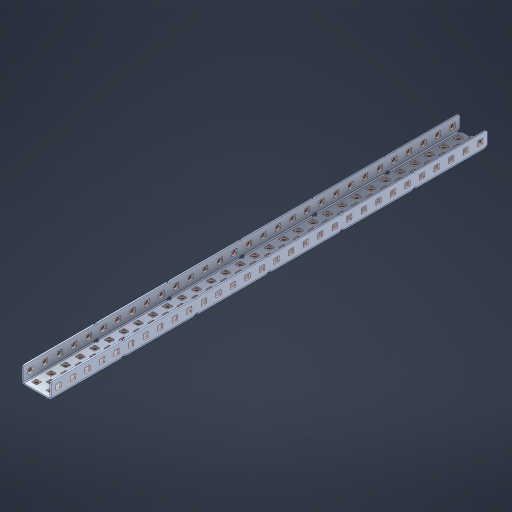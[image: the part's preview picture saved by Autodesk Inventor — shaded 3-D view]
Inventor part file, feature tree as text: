
AUTODESK INVENTOR PART (.ipt)
format: ipt  version: 2023 (Build 270158000, 158)  size: 1,864,704 bytes
history: native  units: in
note: dims shown in document units (in); Inventor stores cm internally (conversion verified against a paired STEP export)
features: other x157, extrude x148, sheet_metal_op x11, sketch x10, pattern_linear x2, mirror x1, chamfer x1
ambient origin geometry x8: Origin, YZ Plane, XZ Plane, XY Plane, X Axis, Y Axis, Z Axis, Center Point
bodies: Solid1 (feature_tree), Body (feature_tree)
feature tree (330):
  sheet_metal_op  "Flanges"
  other  "Flange Pattern Plane"
  other  "Flange Pattern Sketch"
  sheet_metal_op  "Flange Pattern"
  sheet_metal_op  "Body Pattern"
  pattern_linear  "Center Pattern"  Spacing1=0.0469in  [1 undecoded]
  other  "Arc Length"
  mirror  "Notch Mirror"
  pattern_linear  "Notch Pattern"  Spacing1=0.182in  [1 undecoded]
  chamfer  "End Chamfer"
  extrude  "Half Cut"  Depth=0.02in
  sketch  "Sketch1"  dims[d0=1.0in]
  other  "Plate1"
  sketch  "Sketch2"  dims[d1=15.0in]
  other  "Plate2"
  sheet_metal_op  "Bend1"
  sheet_metal_op  "Corner1"
  sketch  "Sketch3"  dims[d2=0.0469in]
  sketch  "Sketch7"  dims[d3=0.0469in]
  other  "Srf1"
  other  "Srf2"
  sketch  "Sketch8"  dims[d4=0.0234in]
  sketch  "Sketch9"  dims[d5=0.0938in]
  other  "Srf91"
  sheet_metal_op  "Body Pattern Sketch"
  other  "Srf92"
  sketch  "Sketch13"  dims[d6=0.0469in]
  sketch  "Sketch14"  dims[d7=0.5in d8=90.0deg d9=0.0312in]
  sketch  "Sketch15"  dims[d10=0.1875in]
  sketch  "Sketch16"  dims[d11=0.0469in d12=0.0469in d16=0.182in d17=0.02in d18=0.0469in d19=0.0in d20=0.25in d21=0.25in d38=11.811in d40=0.5in d41=0.7874in d43=1.0in d46=0.172in d47=1.0in d48=0.0in d49=0.182in d50=0.02in d51=0.25in d52=0.25in d53=0.0469in d54=0.0in d55=0.172in d56=1.0in d57=0.0in d58=0.25in d60=11.811in d62=0.5in d63=0.7874in d65=0.5in d85=0.1227in d86=0.1659in d88=0.04in d89=0.0469in d90=0.0in d91=0.04in d92=0.0491in d95=2.5in d96=0.04in d97=0.25in d98=45.0deg d99=0.25in d100=0.5in d101=0.0in d102=2.497in d106=0.182in d107=0.02in d108=0.5in d109=0.5in d110=0.0469in d111=0.0in d112=0.172in d113=0.5in d114=0.0in d117=0.5in d118=0.5in d119=0.5in]
  other  "Srf786"
  other  "Srf823"
  other  "Srf824"
  other  "Srf825"
  other  "Srf826"
  other  "Srf827"
  other  "Srf828"
  other  "Srf829"
  other  "Srf856"
  other  "Srf857"
  other  "Srf858"
  other  "Srf859"
  other  "Srf860"
  other  "Srf861"
  other  "Srf862"
  other  "Srf889"
  other  "Srf890"
  other  "Srf891"
  other  "Srf892"
  other  "Srf893"
  other  "Srf894"
  other  "Srf895"
  other  "Srf896"
  other  "Srf922"
  other  "Srf923"
  other  "Srf924"
  other  "Srf925"
  other  "Srf926"
  other  "Srf959"
  other  "Srf960"
  other  "Srf961"
  other  "Srf962"
  other  "Srf963"
  other  "Srf996"
  other  "Srf997"
  other  "Srf998"
  other  "Srf999"
  other  "Srf1000"
  other  "Srf1143"
  other  "Srf1144"
  other  "Srf1145"
  other  "Srf1146"
  other  "Srf1147"
  other  "Srf1148"
  other  "Srf1149"
  other  "Srf1150"
  other  "Srf1151"
  other  "Srf1152"
  other  "Srf1153"
  other  "Srf1154"
  other  "Srf1155"
  other  "Srf1156"
  other  "Srf1157"
  other  "Srf1158"
  other  "Srf1159"
  other  "Srf1160"
  other  "Srf1161"
  other  "Srf1162"
  other  "Srf1163"
  other  "Srf1164"
  other  "Srf1165"
  other  "Srf1166"
  other  "Srf1167"
  other  "Srf1168"
  other  "Srf1169"
  other  "Srf1170"
  other  "Srf1171"
  other  "Srf1172"
  other  "Srf1173"
  other  "Srf1174"
  other  "Srf1175"
  other  "Srf1176"
  other  "Srf1177"
  other  "Srf1178"
  other  "Srf1179"
  other  "Srf1180"
  other  "Srf1181"
  other  "Srf1182"
  other  "Srf1183"
  other  "Srf1184"
  other  "Srf1185"
  other  "Srf1186"
  other  "Srf1187"
  other  "Srf1188"
  other  "Srf1199"
  other  "Srf1200"
  other  "Srf1201"
  other  "Srf1202"
  other  "Srf1203"
  other  "Srf1204"
  other  "Srf1205"
  other  "Srf1206"
  other  "Srf1207"
  other  "Srf1208"
  other  "Srf1209"
  other  "Srf1210"
  other  "Srf1211"
  other  "Srf1212"
  other  "Srf1213"
  other  "Srf1214"
  other  "Srf1215"
  other  "Srf1216"
  other  "Srf1217"
  other  "Srf1218"
  other  "Srf1219"
  other  "Srf1220"
  other  "Srf1221"
  other  "Srf1222"
  other  "Srf1223"
  other  "Srf1224"
  other  "Srf1225"
  other  "Srf1226"
  other  "Srf1227"
  other  "Srf1228"
  other  "Srf1229"
  other  "Srf1230"
  other  "Srf1231"
  other  "Srf1232"
  other  "Srf1233"
  other  "Srf1234"
  other  "Srf1235"
  other  "Srf1236"
  other  "Srf1237"
  other  "Srf1238"
  other  "Srf1239"
  other  "Srf1240"
  other  "Srf1241"
  other  "Srf1242"
  other  "Srf1243"
  other  "Srf1244"
  other  "Srf1255"
  other  "Srf1256"
  other  "Srf1257"
  other  "Srf1258"
  other  "Srf1259"
  other  "Srf1260"
  other  "Srf1261"
  other  "Srf1262"
  other  "Srf1263"
  other  "Srf1264"
  other  "Srf1265"
  other  "Srf1266"
  other  "Srf1267"
  other  "Srf1268"
  other  "Srf1269"
  other  "Srf1270"
  sheet_metal_op  "Flange Stamp"
  sheet_metal_op  "Flange Circle"
  sheet_metal_op  "Body Stamp"
  sheet_metal_op  "Body Circle"
  other  "Center Stamp"
  other  "Center Circle"
  sheet_metal_op  "Notch"
  extrude  "ExtrusionSrf2"  Depth=0.0469in
  extrude  "ExtrusionSrf92"  TaperAngle=0.0deg  [1 undecoded]
  extrude  "ExtrusionSrf823"  Depth=0.5in
  extrude  "ExtrusionSrf824"  Depth=0.5in
  extrude  "ExtrusionSrf825"  Depth=0.5in
  extrude  "ExtrusionSrf826"  Depth=0.5in
  extrude  "ExtrusionSrf827"  Depth=1.0in TaperAngle=0.0deg
  extrude  "ExtrusionSrf828"  Depth=0.5in
  extrude  "ExtrusionSrf829"  Depth=0.02in
  extrude  "ExtrusionSrf856"  Depth=0.5in
  extrude  "ExtrusionSrf857"  Depth=0.5in
  extrude  "ExtrusionSrf858"  Depth=0.0469in
  extrude  "ExtrusionSrf859"  TaperAngle=0.0deg  [1 undecoded]
  extrude  "ExtrusionSrf860"  Depth=0.5in
  extrude  "ExtrusionSrf861"  Depth=1.0in TaperAngle=0.0deg
  extrude  "ExtrusionSrf862"  Depth=0.5in
  extrude  "ExtrusionSrf889"  Depth=0.5in
  extrude  "ExtrusionSrf890"  Depth=0.5in
  extrude  "ExtrusionSrf891"  Depth=0.5in
  extrude  "ExtrusionSrf892"  Depth=0.5in
  extrude  "ExtrusionSrf893"  Depth=0.5in
  extrude  "ExtrusionSrf894"  Depth=0.0469in
  extrude  "ExtrusionSrf895"  TaperAngle=0.0deg  [1 undecoded]
  extrude  "ExtrusionSrf896"  Depth=0.5in
  extrude  "ExtrusionSrf922"  Depth=0.5in
  extrude  "ExtrusionSrf923"  Depth=2.5in
  extrude  "ExtrusionSrf924"  Depth=0.5in TaperAngle=45.0deg
  extrude  "ExtrusionSrf925"  Depth=0.5in
  extrude  "ExtrusionSrf926"  Depth=0.5in TaperAngle=0.0deg
  extrude  "ExtrusionSrf959"  Depth=0.5in
  extrude  "ExtrusionSrf960"  Depth=0.5in
  extrude  "ExtrusionSrf961"  Depth=0.02in
  extrude  "ExtrusionSrf962"  Depth=0.5in
  extrude  "ExtrusionSrf963"  Depth=0.5in
  extrude  "ExtrusionSrf996"  Depth=0.0469in
  extrude  "ExtrusionSrf997"  TaperAngle=0.0deg  [1 undecoded]
  extrude  "ExtrusionSrf998"  Depth=0.5in
  extrude  "ExtrusionSrf999"  Depth=0.5in TaperAngle=0.0deg
  extrude  "ExtrusionSrf1000"  Depth=0.5in
  extrude  "ExtrusionSrf1143"  Depth=0.5in
  extrude  "ExtrusionSrf1144"  Depth=0.5in
  extrude  "ExtrusionSrf1145"  [1 undecoded]
  extrude  "ExtrusionSrf1146"  [1 undecoded]
  extrude  "ExtrusionSrf1147"  [1 undecoded]
  extrude  "ExtrusionSrf1148"  [1 undecoded]
  extrude  "ExtrusionSrf1149"  [1 undecoded]
  extrude  "ExtrusionSrf1150"  [1 undecoded]
  extrude  "ExtrusionSrf1151"  [1 undecoded]
  extrude  "ExtrusionSrf1152"  [1 undecoded]
  extrude  "ExtrusionSrf1153"  [1 undecoded]
  extrude  "ExtrusionSrf1154"  [1 undecoded]
  extrude  "ExtrusionSrf1155"  [1 undecoded]
  extrude  "ExtrusionSrf1156"  [1 undecoded]
  extrude  "ExtrusionSrf1157"  [1 undecoded]
  extrude  "ExtrusionSrf1158"  [1 undecoded]
  extrude  "ExtrusionSrf1159"  [1 undecoded]
  extrude  "ExtrusionSrf1160"  [1 undecoded]
  extrude  "ExtrusionSrf1161"  [1 undecoded]
  extrude  "ExtrusionSrf1162"  [1 undecoded]
  extrude  "ExtrusionSrf1163"  [1 undecoded]
  extrude  "ExtrusionSrf1164"  [1 undecoded]
  extrude  "ExtrusionSrf1165"  [1 undecoded]
  extrude  "ExtrusionSrf1166"  [1 undecoded]
  extrude  "ExtrusionSrf1167"  [1 undecoded]
  extrude  "ExtrusionSrf1168"  [1 undecoded]
  extrude  "ExtrusionSrf1169"  [1 undecoded]
  extrude  "ExtrusionSrf1170"  [1 undecoded]
  extrude  "ExtrusionSrf1171"  [1 undecoded]
  extrude  "ExtrusionSrf1172"  [1 undecoded]
  extrude  "ExtrusionSrf1173"  [1 undecoded]
  extrude  "ExtrusionSrf1174"  [1 undecoded]
  extrude  "ExtrusionSrf1175"  [1 undecoded]
  extrude  "ExtrusionSrf1176"  [1 undecoded]
  extrude  "ExtrusionSrf1177"  [1 undecoded]
  extrude  "ExtrusionSrf1178"  [1 undecoded]
  extrude  "ExtrusionSrf1179"  [1 undecoded]
  extrude  "ExtrusionSrf1180"  [1 undecoded]
  extrude  "ExtrusionSrf1181"  [1 undecoded]
  extrude  "ExtrusionSrf1182"  [1 undecoded]
  extrude  "ExtrusionSrf1183"  [1 undecoded]
  extrude  "ExtrusionSrf1184"  [1 undecoded]
  extrude  "ExtrusionSrf1185"  [1 undecoded]
  extrude  "ExtrusionSrf1186"  [1 undecoded]
  extrude  "ExtrusionSrf1187"  [1 undecoded]
  extrude  "ExtrusionSrf1188"  [1 undecoded]
  extrude  "ExtrusionSrf1199"  [1 undecoded]
  extrude  "ExtrusionSrf1200"  [1 undecoded]
  extrude  "ExtrusionSrf1201"  [1 undecoded]
  extrude  "ExtrusionSrf1202"  [1 undecoded]
  extrude  "ExtrusionSrf1203"  [1 undecoded]
  extrude  "ExtrusionSrf1204"  [1 undecoded]
  extrude  "ExtrusionSrf1205"  [1 undecoded]
  extrude  "ExtrusionSrf1206"  [1 undecoded]
  extrude  "ExtrusionSrf1207"  [1 undecoded]
  extrude  "ExtrusionSrf1208"  [1 undecoded]
  extrude  "ExtrusionSrf1209"  [1 undecoded]
  extrude  "ExtrusionSrf1210"  [1 undecoded]
  extrude  "ExtrusionSrf1211"  [1 undecoded]
  extrude  "ExtrusionSrf1212"  [1 undecoded]
  extrude  "ExtrusionSrf1213"  [1 undecoded]
  extrude  "ExtrusionSrf1214"  [1 undecoded]
  extrude  "ExtrusionSrf1215"  [1 undecoded]
  extrude  "ExtrusionSrf1216"  [1 undecoded]
  extrude  "ExtrusionSrf1217"  [1 undecoded]
  extrude  "ExtrusionSrf1218"  [1 undecoded]
  extrude  "ExtrusionSrf1219"  [1 undecoded]
  extrude  "ExtrusionSrf1220"  [1 undecoded]
  extrude  "ExtrusionSrf1221"  [1 undecoded]
  extrude  "ExtrusionSrf1222"  [1 undecoded]
  extrude  "ExtrusionSrf1223"  [1 undecoded]
  extrude  "ExtrusionSrf1224"  [1 undecoded]
  extrude  "ExtrusionSrf1225"  [1 undecoded]
  extrude  "ExtrusionSrf1226"  [1 undecoded]
  extrude  "ExtrusionSrf1227"  [1 undecoded]
  extrude  "ExtrusionSrf1228"  [1 undecoded]
  extrude  "ExtrusionSrf1229"  [1 undecoded]
  extrude  "ExtrusionSrf1230"  [1 undecoded]
  extrude  "ExtrusionSrf1231"  [1 undecoded]
  extrude  "ExtrusionSrf1232"  [1 undecoded]
  extrude  "ExtrusionSrf1233"  [1 undecoded]
  extrude  "ExtrusionSrf1234"  [1 undecoded]
  extrude  "ExtrusionSrf1235"  [1 undecoded]
  extrude  "ExtrusionSrf1236"  [1 undecoded]
  extrude  "ExtrusionSrf1237"  [1 undecoded]
  extrude  "ExtrusionSrf1238"  [1 undecoded]
  extrude  "ExtrusionSrf1239"  [1 undecoded]
  extrude  "ExtrusionSrf1240"  [1 undecoded]
  extrude  "ExtrusionSrf1241"  [1 undecoded]
  extrude  "ExtrusionSrf1242"  [1 undecoded]
  extrude  "ExtrusionSrf1243"  [1 undecoded]
  extrude  "ExtrusionSrf1244"  [1 undecoded]
  extrude  "ExtrusionSrf1255"  [1 undecoded]
  extrude  "ExtrusionSrf1256"  [1 undecoded]
  extrude  "ExtrusionSrf1257"  [1 undecoded]
  extrude  "ExtrusionSrf1258"  [1 undecoded]
  extrude  "ExtrusionSrf1259"  [1 undecoded]
  extrude  "ExtrusionSrf1260"  [1 undecoded]
  extrude  "ExtrusionSrf1261"  [1 undecoded]
  extrude  "ExtrusionSrf1262"  [1 undecoded]
  extrude  "ExtrusionSrf1263"  [1 undecoded]
  extrude  "ExtrusionSrf1264"  [1 undecoded]
  extrude  "ExtrusionSrf1265"  [1 undecoded]
  extrude  "ExtrusionSrf1266"  [1 undecoded]
  extrude  "ExtrusionSrf1267"  [1 undecoded]
  extrude  "ExtrusionSrf1268"  [1 undecoded]
  extrude  "ExtrusionSrf1269"  [1 undecoded]
  extrude  "ExtrusionSrf1270"  [1 undecoded]
note: 112 required parameter values undecoded (feature->parameter linkage not recoverable at this tier; creation-order binding heuristic only, values carry confidence <= 0.55)
